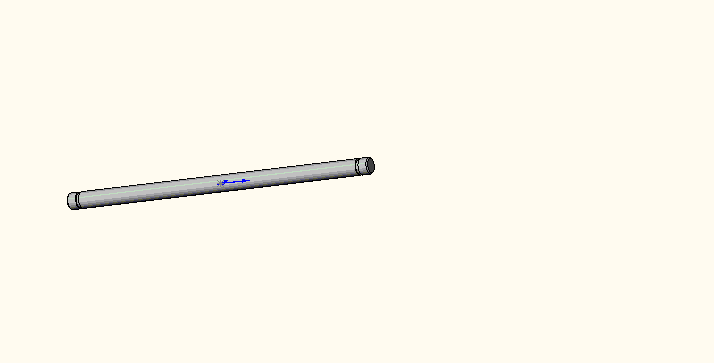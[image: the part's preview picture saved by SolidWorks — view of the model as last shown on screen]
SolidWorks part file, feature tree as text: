
SOLIDWORKS PART (.sldprt)
format: sldprt  version: not decoded by parser v0  size: 182,784 bytes
history: native  units: mm
features: sketch x2, material x1, extrude x1, cut_revolve x1, chamfer x1 (+10 scaffold rows collapsed)
feature tree (16):
  scaffold x10  (default folders/planes/origin — collapsed)
  material  "Material <not specified>"
  sketch  "Sketch1"  dims[D1=1.5875mm]
  extrude  "Extrude1"  Depth=31.75mm
  sketch  "Sketch2"  dims[D1=0.3048mm D2=0.127mm D3=1.27mm]
  cut_revolve  "Cut-Revolve1"  Angle=360deg
  chamfer  "Chamfer1"  Distance=0.127mm Angle=45deg
decode coverage: 5 of 5 modeling features carry decoded parameters
note: suppression state not decoded; provenance and decode notes live in map.json
